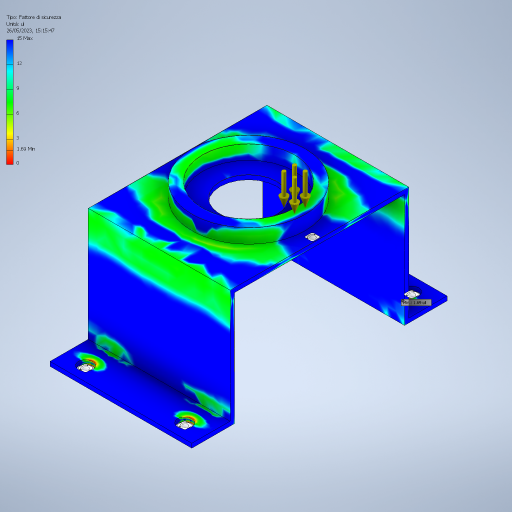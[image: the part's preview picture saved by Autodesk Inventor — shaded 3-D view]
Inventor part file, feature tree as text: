
AUTODESK INVENTOR PART (.ipt)
format: ipt  version: 2023 (Build 270158000, 158)  size: 396,800 bytes
history: native  units: mm
features: sketch x5, extrude x4
ambient origin geometry x8: Origin, YZ Plane, XZ Plane, XY Plane, X Axis, Y Axis, Z Axis, Center Point
bodies: Solido1 (feature_tree)
feature tree (9):
  extrude  "Estrusione1"  Depth=30.0mm
  sketch  "Schizzo2"
  extrude  "Estrusione2"  Depth=120.0mm
  extrude  "Estrusione3"  Depth=3.0mm
  extrude  "Estrusione4"  Depth=3.0mm
  sketch  "Schizzo4"
  sketch  "Schizzo5"
  sketch  "Schizzo1"
  sketch  "Schizzo3"
